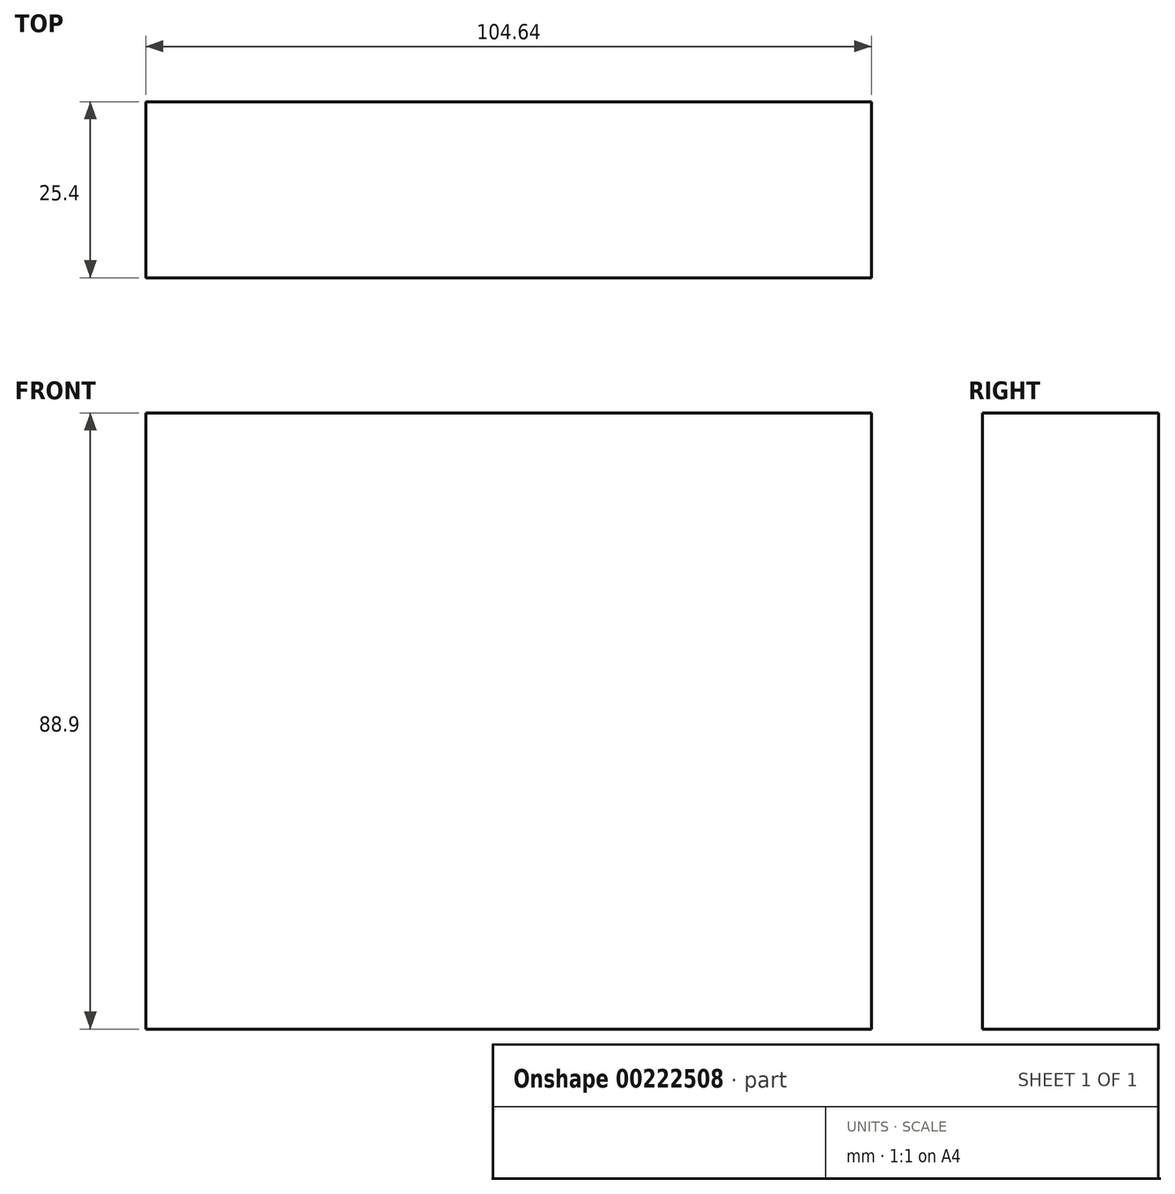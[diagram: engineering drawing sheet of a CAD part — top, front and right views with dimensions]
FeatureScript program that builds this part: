
annotation { "Feature Type Name" : "Feature", "Feature Type Description" : "" }
export const myFeature = defineFeature(function(context is Context, id is Id, definition is map)
    precondition{}
    {
        {
            var Q0;
            Q0=qCreatedBy(makeId("Front.planeOp"),FACE);
            var sketch = newSketch(context, id + "F0", { "sketchPlane" : qUnion([Q0])});
            skLineSegment(sketch, "E0.bottom", {"start": v(52.32, 44.45) * mm, "end": v(-52.32, 44.45) * mm});
            skLineSegment(sketch, "E0.top", {"start": v(52.32, -44.45) * mm, "end": v(-52.32, -44.45) * mm});
            skLineSegment(sketch, "E0.left", {"start": v(52.32, 44.45) * mm, "end": v(52.32, -44.45) * mm});
            skLineSegment(sketch, "E0.right", {"start": v(-52.32, 44.45) * mm, "end": v(-52.32, -44.45) * mm});
            skPoint(sketch, "E0.middle", {"position": v(0, 0) * mm});
            skSolve(sketch);
        }
        {
            var Q0;
            Q0 = qSketchRegion(id + "F0", true);
            extrude(context, id + "F1", {"entities" : qUnion([Q0]), "depth" : 25.4 * mm});
        }
    });
